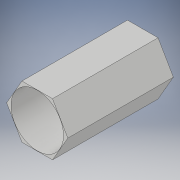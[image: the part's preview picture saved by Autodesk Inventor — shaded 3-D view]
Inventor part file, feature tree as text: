
AUTODESK INVENTOR PART (.ipt)
format: ipt  version: 2017 (Build 210142000, 142)  size: 97,280 bytes
history: native  units: in
note: dims shown in document units (in); Inventor stores cm internally (conversion verified against a paired STEP export)
features: extrude x1, sketch x1
ambient origin geometry x8: Origin, YZ Plane, XZ Plane, XY Plane, X Axis, Y Axis, Z Axis, Center Point
bodies: Solid1 (feature_tree)
feature tree (2):
  extrude  "Extrusion1"  Depth=1.0in TaperAngle=0.0deg
  sketch  "Sketch1"  dims[d0=0.498in d1=1.0in d2=0.0in]
